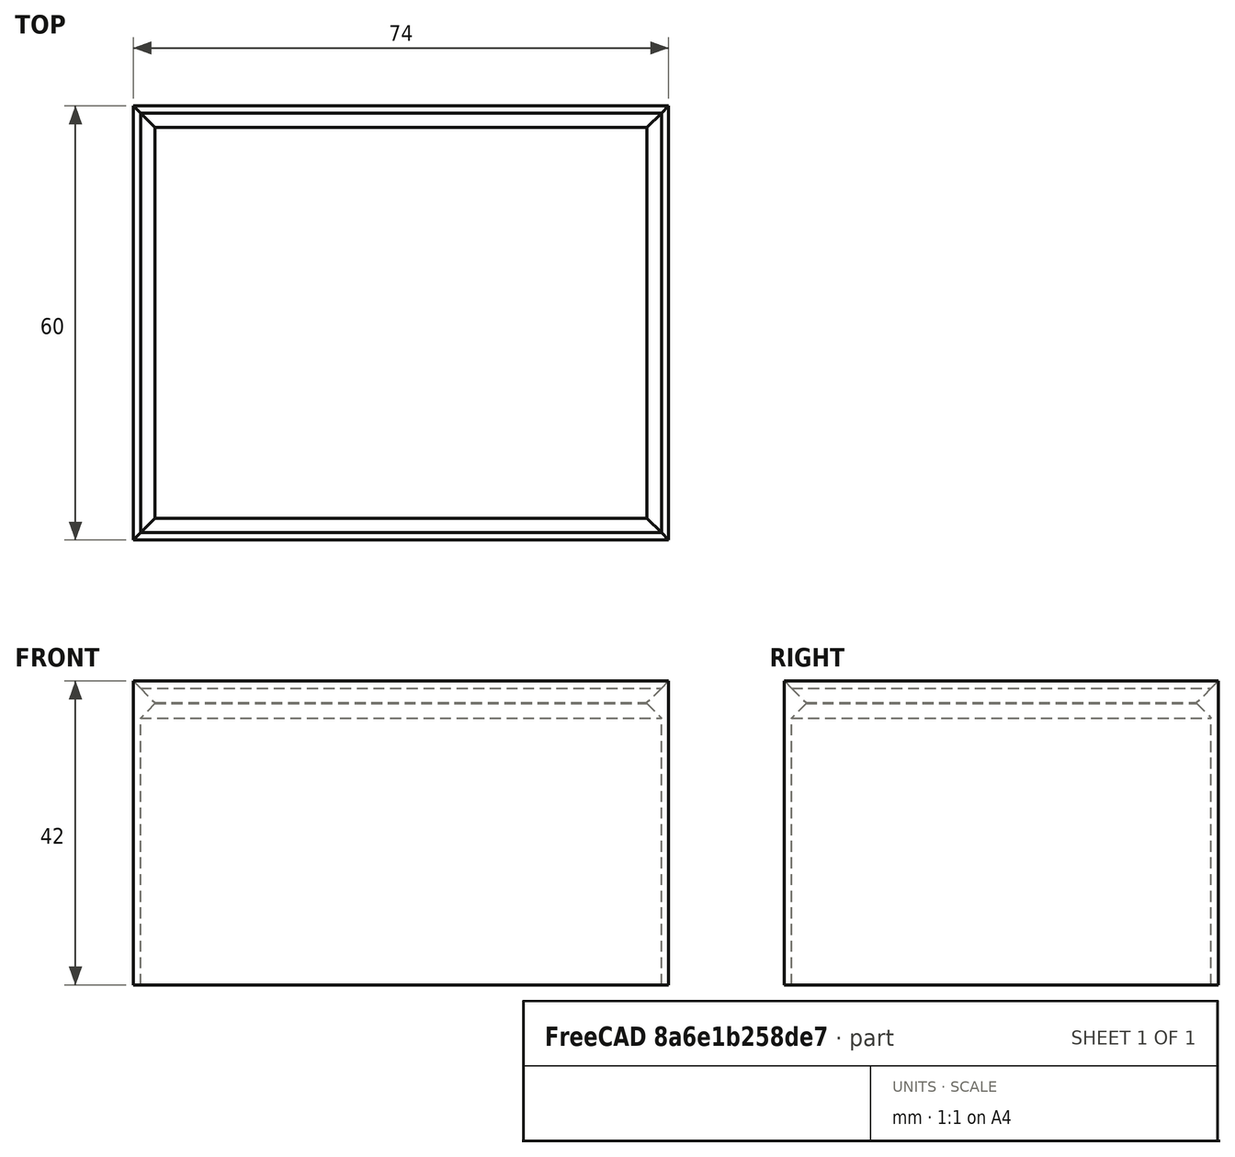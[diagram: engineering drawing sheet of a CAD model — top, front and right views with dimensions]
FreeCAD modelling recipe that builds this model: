
FCSTD DOCUMENT  (FreeCAD 0.16R)
Label: sonoff-T1-US-Steckdose_Deckel
License: All rights reserved
LicenseURL: http://en.wikipedia.org/wiki/All_rights_reserved
objects: Part::Box×4, Part::Chamfer×3, Part::Cut×2, Part::Fuse×1
note: 10 computed .brp shape members not serialized (recipe doc carries the construction recipe); baked Part::Feature solids carry a one-line shape summary decoded from their .brp

FEATURE [Part::Box] Box032  label="Basis Stecker"
  Height = 42
  Length = 74
  Placement = pos=(0,-60,0) rot=(0,0,1;0rad)
  Width = 60
FEATURE [Part::Box] Box033  label="Ausschnitt Stecker"
  Height = 42
  Length = 72
  Placement = pos=(1,-59,0) rot=(0,0,1;0rad)
  Width = 58
FEATURE [Part::Cut] Cut014
  Base = -> Box032
  Tool = -> Box033
FEATURE [Part::Chamfer] Chamfer020
  Base = -> Cut014
  Edges = 4 edges r=0.99: [Edge10,Edge11,Edge12,Edge13]
FEATURE [Part::Box] Box038  label="Kragen Stecker"
  Height = 4.1
  Length = 74
  Placement = pos=(0,-60,0) rot=(0,0,1;0rad)
  Width = 60
FEATURE [Part::Box] Box039  label="Kragen Stecker Ausschnitt"
  Height = 4.1
  Length = 68
  Placement = pos=(3,-57,0) rot=(0,0,1;0rad)
  Width = 54
FEATURE [Part::Cut] Cut019
  Base = -> Box038
  Placement = pos=(0,0,36.9) rot=(0,0,1;0rad)
  Tool = -> Box039
FEATURE [Part::Chamfer] Chamfer021
  Base = -> Cut019
  Edges = 4 edges r=2: [Edge10,Edge11,Edge12,Edge13]
FEATURE [Part::Chamfer] Chamfer022
  Base = -> Chamfer021
  Edges = 4 edges r=2: [Edge26,Edge29,Edge31,Edge32]
FEATURE [Part::Fuse] Fusion  label="Form"
  Base = -> Chamfer020
  Tool = -> Chamfer022
